# Revit family: NXOS_Series
name_source: partatom
category: Lighting Devices
units: mm (PartAtom-declared; Revit-internal decimal feet)

## family parameters
Cut with Voids When Loaded = No
Host = Face
Maintain Annotation Orientation = Yes
OmniClass Number = 23.85.80.11.27
OmniClass Title = Lighting Controls
Part Type = Normal
Room Calculation Point = No
Round Connector Dimension = Use Diameter
Shared = No

## types (1)
- NXOS Series
    Assembly Code = D5020
    Certifications = UL and cUL listed
    Connector Description 1 = Power Supply
    Connector Description 2 = Controls
    Coverage = Ceiling mount sensor: 500 sq. ft. (Major motion) / 250 sq. ft. (Minor motion) to 2000 sq. ft. (Major motion)
    Default Elevation = 48 "
    Description = Ceiling Mount Occupancy Sensors
    Device Material = Plastic - White
    Frequency = 40000 Hz
    Glass = Plastic -  Polyethylene
    Load Classification = Lighting
    Manufacturer = NX Lighting Controls
    Model = NXOS Series
    Mounting = Mounting base provided, Recommended MAX mounting height:12 ft. [3.66 m]
    Operating Temperature = 32° to + 104° [0° +40°]
    Passive Infrared = Dual element pyrometer and 12 element cylindrical rugged lens
    Power Requirements = Powered by NX Room Controller using plenum rated CAT5 cables
    Relative humidity = 0 to 95%
    Timer Timeout = Automatic mode: 8-30 min. Test mode: 8 seconds
    Type Comments = Lighting Device
    URL = https://www.currentlighting.com
    Ultrasonic Output = Maximum amount of radiation output allowed:115dB @ 1 ft. [o.30 m] from source
    Warranty = Five-year limited
    Weight = 0 kg

## geometry (parser evidence)
native form markers: Blend x4, Sweep x7
no freeform markers — native parametric forms only
